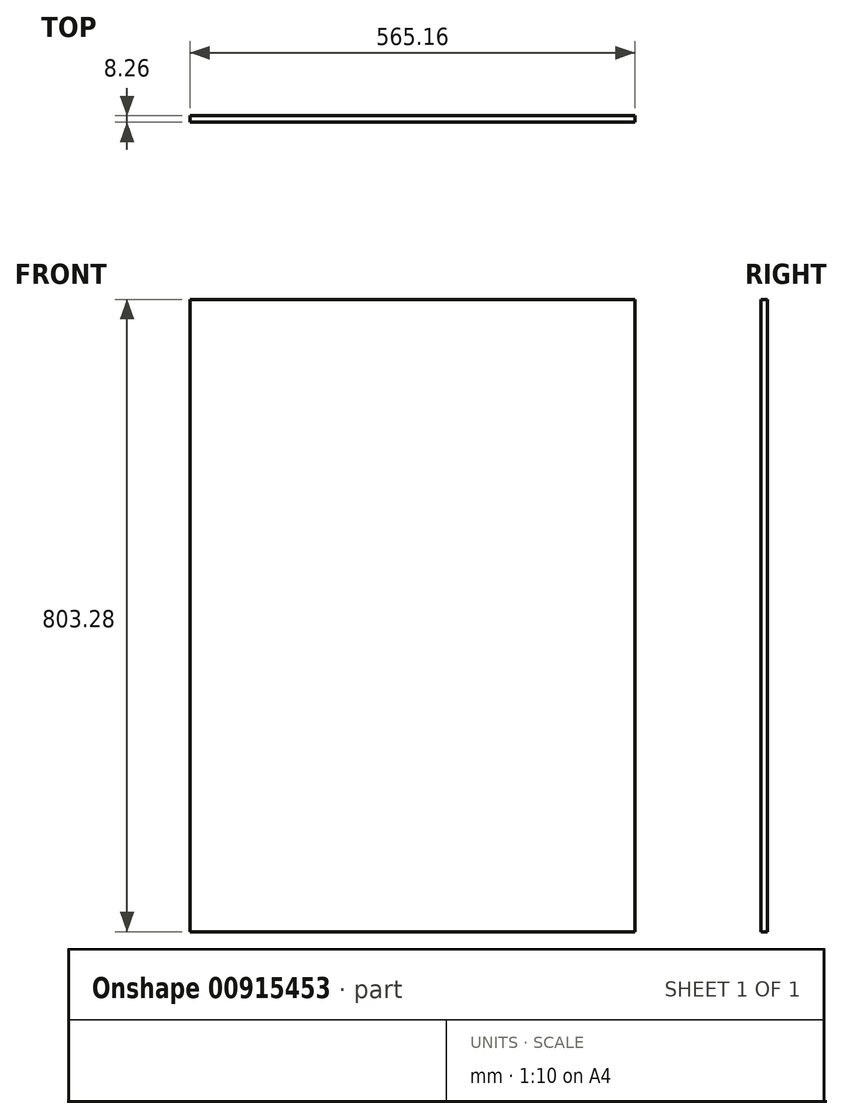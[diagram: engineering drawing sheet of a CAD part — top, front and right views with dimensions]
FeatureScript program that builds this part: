
annotation { "Feature Type Name" : "Feature", "Feature Type Description" : "" }
export const myFeature = defineFeature(function(context is Context, id is Id, definition is map)
    precondition{}
    {
        {
            var Q0;
            Q0=qCreatedBy(makeId("Front.planeOp"),FACE);
            var sketch = newSketch(context, id + "F0", { "sketchPlane" : qUnion([Q0])});
            skLineSegment(sketch, "E0.bottom", {"start": v(282.57, 401.64) * mm, "end": v(-282.58, 401.64) * mm});
            skLineSegment(sketch, "E0.top", {"start": v(282.58, -401.64) * mm, "end": v(-282.57, -401.64) * mm});
            skLineSegment(sketch, "E0.left", {"start": v(282.57, 401.64) * mm, "end": v(282.58, -401.64) * mm});
            skLineSegment(sketch, "E0.right", {"start": v(-282.58, 401.64) * mm, "end": v(-282.57, -401.64) * mm});
            skPoint(sketch, "E0.middle", {"position": v(0, 0) * mm});
            skSolve(sketch);
        }
        {
            var Q0;
            Q0=makeQuery(id+"F0.imprint","IMPRINT",FACE,{"disambiguationData":[TD([[makeQuery(id+"F0.imprint","IMPRINT",EDGE,{"derivedFrom":sQuery(id+"F0.wireOp",EDGE,"E0.bottom")}),1.0]])]});
            extrude(context, id + "F1", {"entities" : qUnion([Q0]), "depth" : 8.25 * mm, "offsetDistance" : 25.4 * mm});
        }
    });
